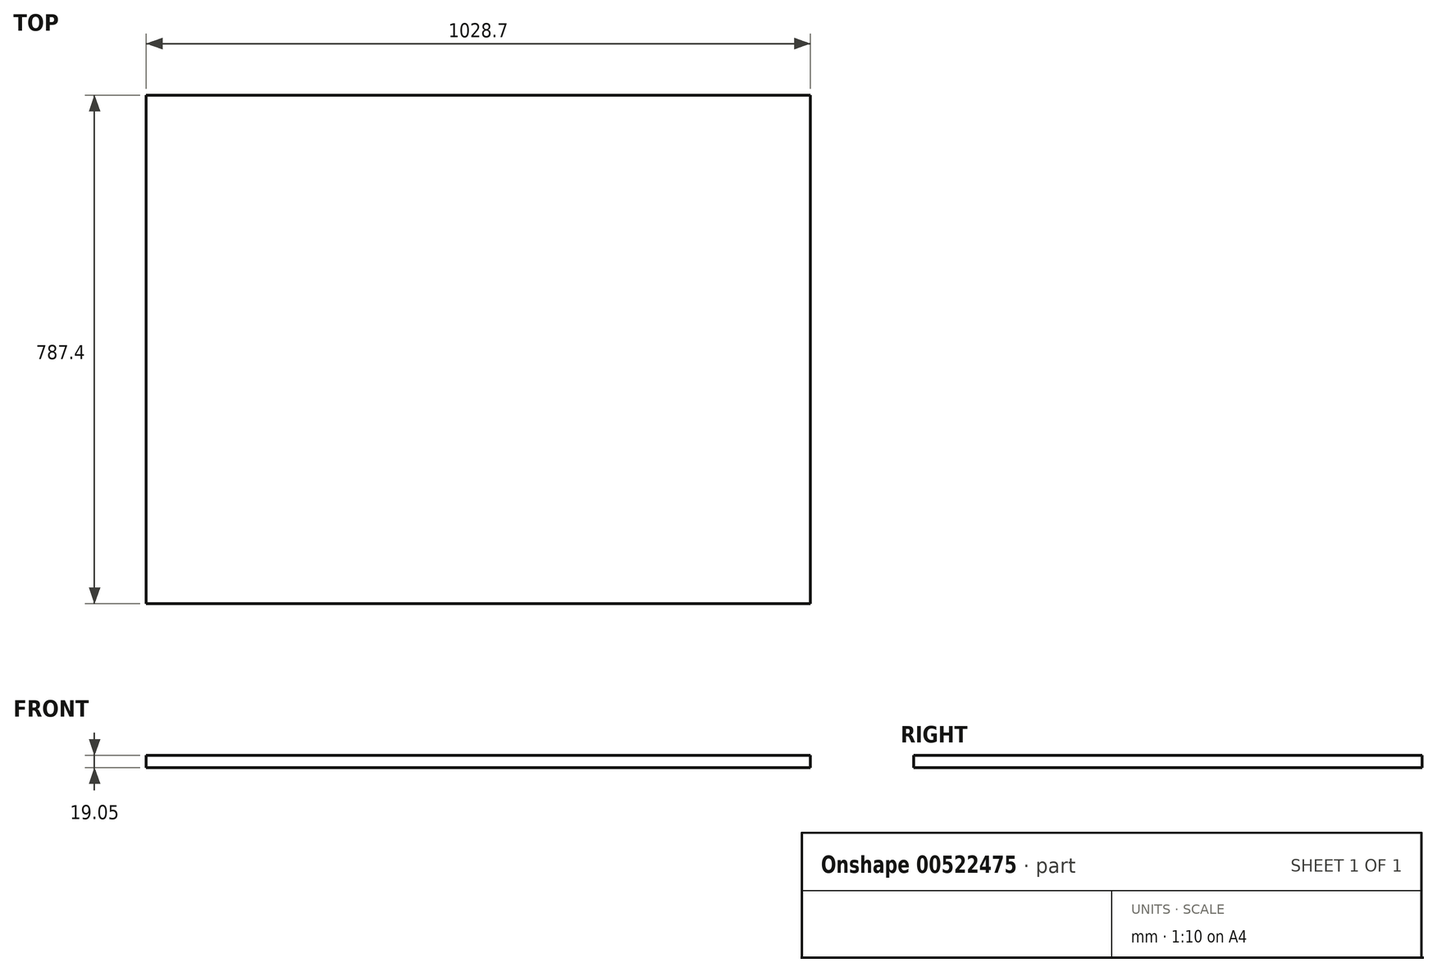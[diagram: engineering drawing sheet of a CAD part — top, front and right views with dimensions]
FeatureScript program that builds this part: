
annotation { "Feature Type Name" : "Feature", "Feature Type Description" : "" }
export const myFeature = defineFeature(function(context is Context, id is Id, definition is map)
    precondition{}
    {
        {
            var Q0;
            Q0=qCreatedBy(makeId("Top.planeOp"),FACE);
            var sketch = newSketch(context, id + "F0", { "sketchPlane" : qUnion([Q0])});
            skLineSegment(sketch, "E0.bottom", {"start": v(-570.57, 532.68) * mm, "end": v(458.13, 532.68) * mm});
            skLineSegment(sketch, "E0.top", {"start": v(-570.57, -254.72) * mm, "end": v(458.13, -254.72) * mm});
            skLineSegment(sketch, "E0.left", {"start": v(-570.57, 532.68) * mm, "end": v(-570.57, -254.72) * mm});
            skLineSegment(sketch, "E0.right", {"start": v(458.13, 532.68) * mm, "end": v(458.13, -254.72) * mm});
            skSolve(sketch);
        }
        {
            var Q0;
            Q0=makeQuery(id+"F0.imprint","IMPRINT",FACE,{"disambiguationData":[TD([[makeQuery(id+"F0.imprint","IMPRINT",EDGE,{"derivedFrom":sQuery(id+"F0.wireOp",EDGE,"E0.bottom")}),-1.0]])]});
            extrude(context, id + "F1", {"entities" : qUnion([Q0]), "depth" : 19.05 * mm, "offsetDistance" : 25.4 * mm});
        }
    });
